# Revit family: Legrand_IP21_transformer_for_three-phase_hospital_rooms
name_source: partatom
category: Installations électriques
revit_build: Autodesk Revit 2018 (Build: 20170223_1515(x64)
units: mm (PartAtom-declared; Revit-internal decimal feet)

## family parameters
Basée sur le plan de construction = Non
Conserver l'orientation des annotations = Non
Cote de connecteur circulaire = Utiliser le diamètre
Couper avec des vides une fois chargée = Non
Numéro OmniClass = 23.80.00.00
Partagée = Non
Point de calcul de pièce = Non
Titre OmniClass = Electric Power and Lighting
Toujours verticalement = Oui
Type d'élément = Normal

## types (4) — shared parameters
Characteristic = Class I - IP21 - IK08
Fabricant = Legrand
General Conditions of Use = https://export.legrand.com
Insulating = class H
Primary voltage = 400V en Y +N
Secondary voltage = 230V en Y +N
Type of transformer = Three-phase 230V N / 230V N
URL = www.legrand.com
fixing diameter = 9 mm  [stored 0.0295276 ft]

## per-type parameters (varying)
| type | 042581 | 042583, 042584, 042585 | Primary Cable Section | Secondary cable section | Ucc (%) | dimension A | dimension B | dimension C | empty loss | fixing F | fixing G | max totaly loss | power | weight |
| Transformer for hospital premises 042585 | Non | Oui | 16 mm² | 16 mm² | 2.7 | 470 mm  [stored 1.54199 ft] | 410 mm  [stored 1.34514 ft] | 340 mm  [stored 1.11549 ft] | 88 W | 450 mm  [stored 1.47638 ft] | 176 mm  [stored 0.577428 ft] | 518 W | 10 kVA | 160.00 kg |
| Transformer for hospital premises 042581 | Oui | Non | 10 mm² | 10 mm² | 2.7 | 420 mm  [stored 1.37795 ft] | 270 mm  [stored 0.885827 ft] | 190 mm  [stored 0.62336 ft] | 50 W | 400 mm  [stored 1.31234 ft] | 126 mm  [stored 0.413386 ft] | 207 W | 4 kVA | 60.00 kg |
| Transformer for hospital premises 042583 | Non | Oui | 10 mm² | 10 mm² | 2.8 | 470 mm  [stored 1.54199 ft] | 410 mm  [stored 1.34514 ft] | 340 mm  [stored 1.11549 ft] | 76 W | 450 mm  [stored 1.47638 ft] | 126 mm  [stored 0.413386 ft] | 308 W | 6 kVA | 82.00 kg |
| Transformer for hospital premises 042584 | Non | Oui | 16 mm² | 16 mm² | 2.7 | 470 mm  [stored 1.54199 ft] | 410 mm  [stored 1.34514 ft] | 340 mm  [stored 1.11549 ft] | 96 W | 450 mm  [stored 1.47638 ft] | 176 mm  [stored 0.577428 ft] | 377 W | 8 kVA | 106.00 kg |

note: [stored X ft] marks values corroborated as IEEE doubles in the binary element streams (Revit-internal decimal feet)
